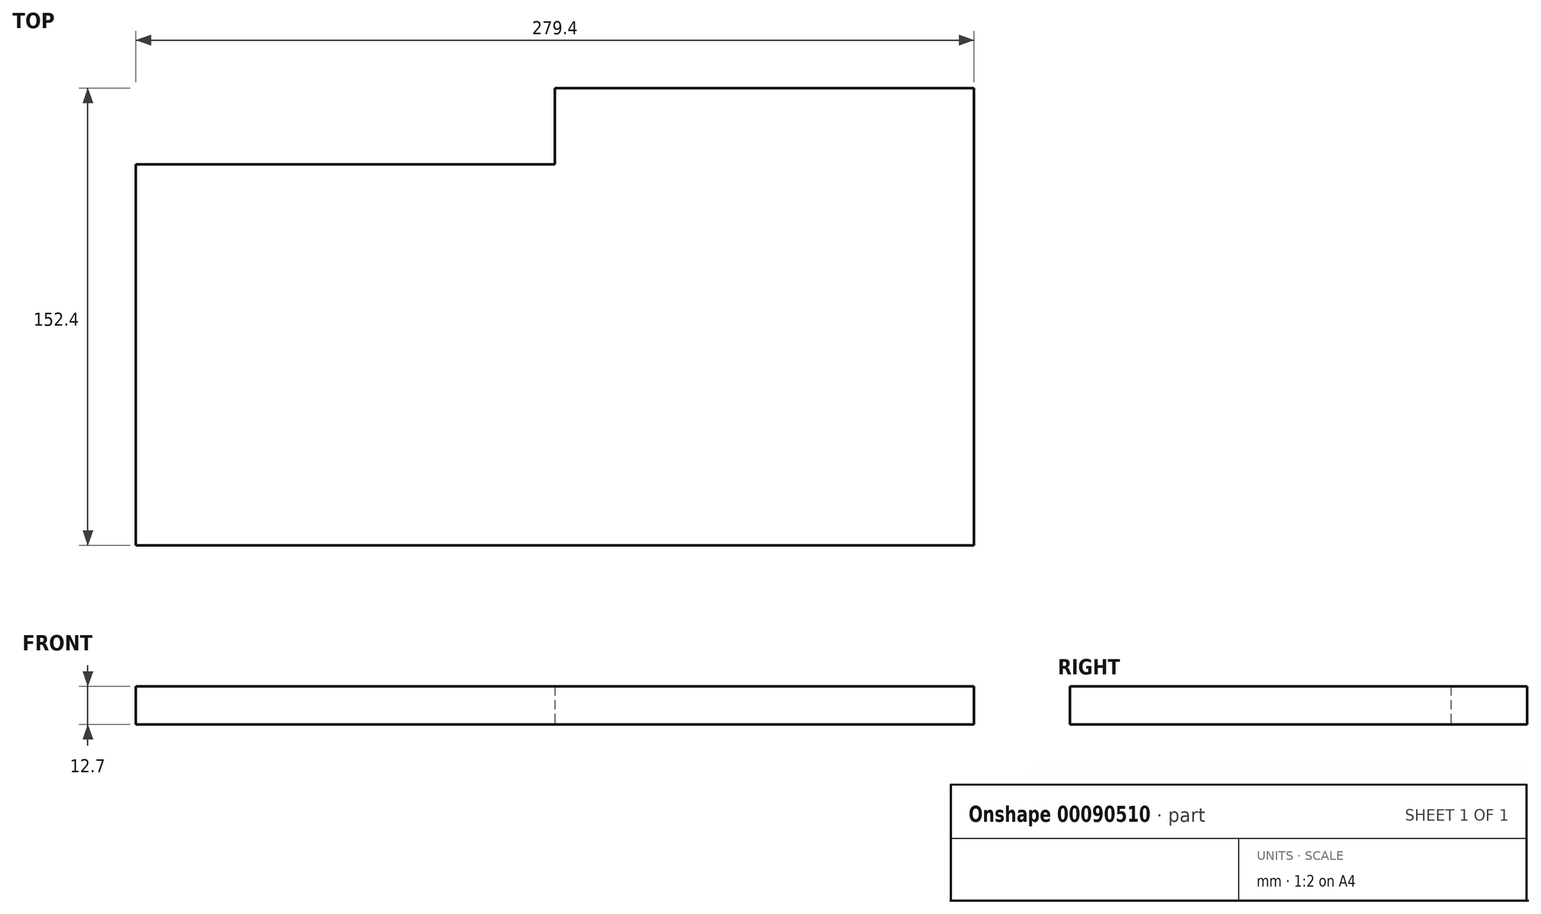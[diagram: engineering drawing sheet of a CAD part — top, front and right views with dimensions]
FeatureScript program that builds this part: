
annotation { "Feature Type Name" : "Feature", "Feature Type Description" : "" }
export const myFeature = defineFeature(function(context is Context, id is Id, definition is map)
    precondition{}
    {
        {
            var Q0;
            Q0=qCreatedBy(makeId("Top.planeOp"),FACE);
            var sketch = newSketch(context, id + "F0", { "sketchPlane" : qUnion([Q0])});
            skLineSegment(sketch, "E0", {"start": v(0, 0) * mm, "end": v(279.4, 0) * mm});
            skLineSegment(sketch, "E1", {"start": v(279.4, 0) * mm, "end": v(279.4, 152.4) * mm});
            skLineSegment(sketch, "E2", {"start": v(279.4, 152.4) * mm, "end": v(139.7, 152.4) * mm});
            skLineSegment(sketch, "E3", {"start": v(139.7, 152.4) * mm, "end": v(139.7, 127) * mm});
            skLineSegment(sketch, "E4", {"start": v(139.7, 127) * mm, "end": v(0, 127) * mm});
            skLineSegment(sketch, "E5", {"start": v(0, 127) * mm, "end": v(0, 0) * mm});
            skSolve(sketch);
        }
        {
            var Q0;
            Q0=makeQuery(id+"F0.imprint","IMPRINT",FACE,{"disambiguationData":[TD([[makeQuery(id+"F0.imprint","IMPRINT",EDGE,{"derivedFrom":sQuery(id+"F0.wireOp",EDGE,"E0")}),1.0]])]});
            extrude(context, id + "F1", {"entities" : qUnion([Q0]), "depth" : 12.7 * mm});
        }
    });
